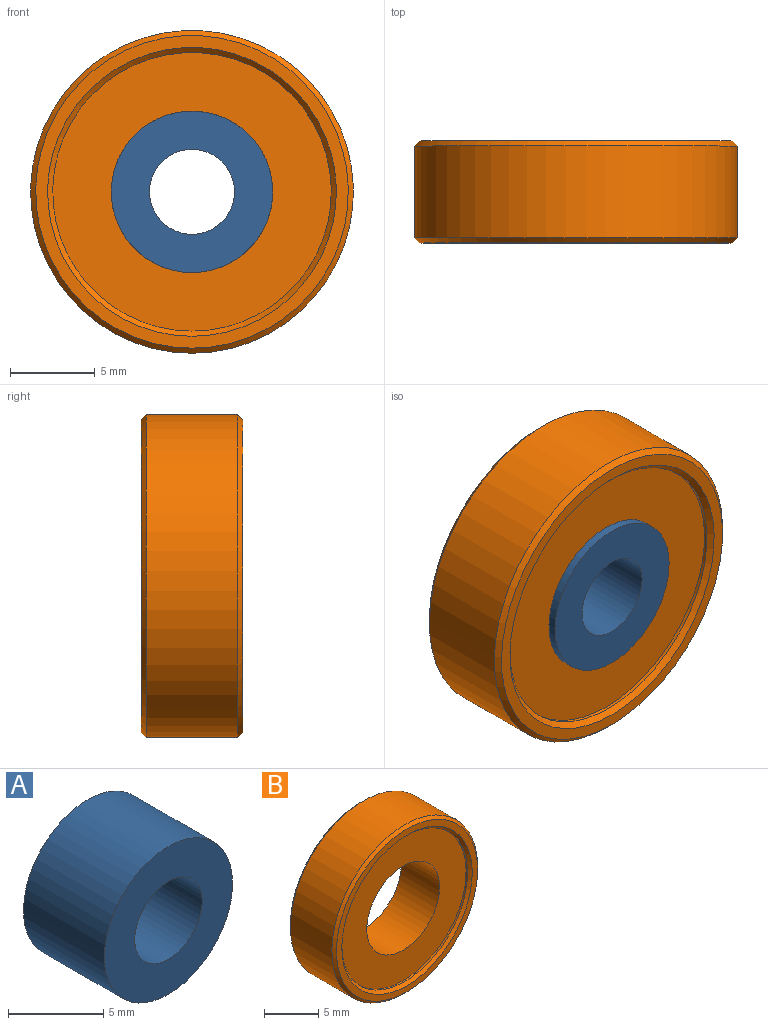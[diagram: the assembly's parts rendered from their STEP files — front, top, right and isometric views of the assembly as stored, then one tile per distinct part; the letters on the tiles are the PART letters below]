
ASSEMBLY  parts=2 mates=1
PART A: 4 faces, bbox 9.5x6x9.5 mm
  f0: cylinder r=2.5mm len=6mm, axis (0,1,0), area 94.2mm2, adj f2,f3
  f1: cylinder r=4.75mm len=9.5mm, axis (0,1,0), area 179.1mm2, adj f2,f3
  f2: plane 9.5x9.5mm, normal (0,-1,0), area 51.2mm2, adj f0,f1
  f3: plane 9.5x9.5mm, normal (0,1,0), area 51.2mm2, adj f0,f1
PART B: 12 faces, bbox 19x6x19 mm
  f0: cylinder r=8.2mm len=16.4mm, axis (0,1,0), area 10.3mm2, adj f7,f8
  f1: cylinder r=8.2mm len=16.4mm, axis (0,1,0), area 10.3mm2, adj f6,f10
  f2: cylinder r=9.5mm len=19mm, axis (0,1,0), area 322.3mm2, adj f9,f11
  f3: plane 18.4x18.4mm, normal (0,-1,0), area 38.9mm2, adj f10,f11
  f4: plane 18.4x18.4mm, normal (0,1,0), area 38.9mm2, adj f8,f9
  f5: cylinder r=4.75mm len=9.5mm, axis (0,1,0), area 149.2mm2, adj f6,f7
  f6: plane 16.4x16.4mm, normal (0,-1,0), area 140.4mm2, adj f1,f5
  f7: plane 16.4x16.4mm, normal (0,1,0), area 140.4mm2, adj f0,f5
  f8: cone r=8.5mm half-angle=45deg, axis (0,1,0), area 22.3mm2, adj f0,f4
  f9: cone r=9.5mm half-angle=45deg, axis (0,-1,0), area 24.9mm2, adj f2,f4
  f10: cone r=8.2mm half-angle=45deg, axis (0,-1,0), area 22.3mm2, adj f1,f3
  f11: cone r=9.2mm half-angle=45deg, axis (0,1,0), area 24.9mm2, adj f2,f3
PLACE A rot(axis=(0,1,0),27.7deg) t=(0,3,0)mm
PLACE B t=(0,3,0)mm
MATE revolute B.f0 <-> A.f0  axis (0,-1,0) through (0,0,0)mm
